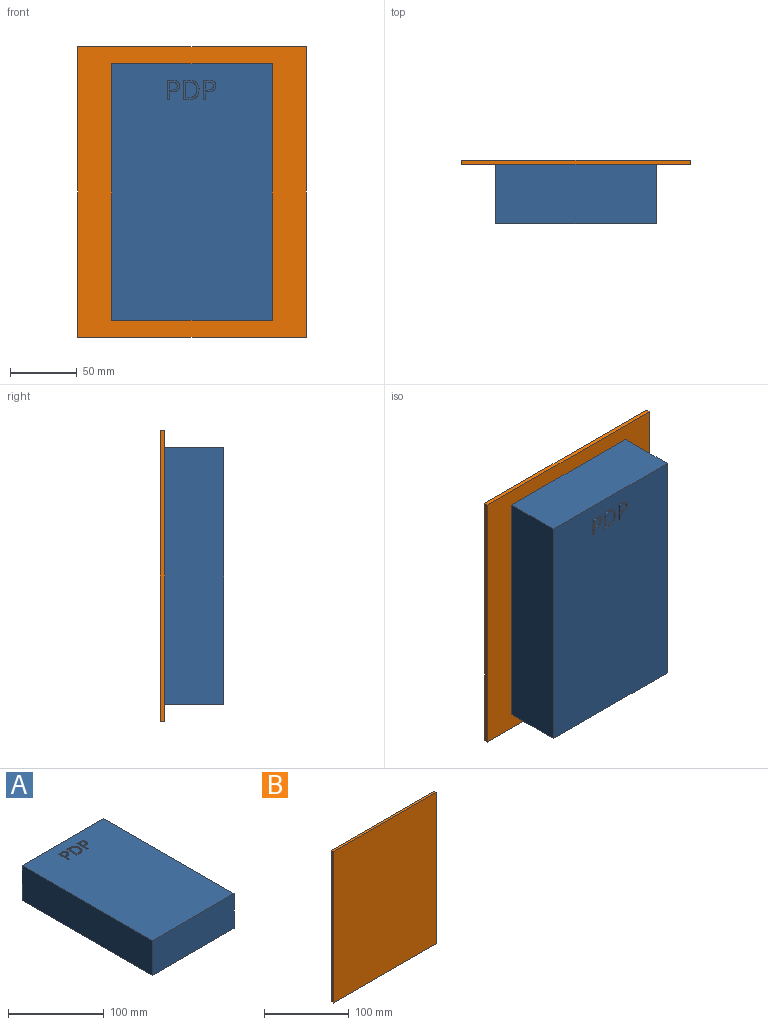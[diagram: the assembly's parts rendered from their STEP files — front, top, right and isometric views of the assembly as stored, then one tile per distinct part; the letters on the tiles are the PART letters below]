
ASSEMBLY  parts=2 mates=1
PART A: 56 faces, bbox 120.9x192.7x44.5 mm
  f0: plane 192.68x120.88mm, normal (0,0,1), area 22972.2mm2, adj f1,f2,f3,f4,f12,f13,f14,f15
  f1: plane 192.68x44.45mm, normal (1,0,0), area 8564.8mm2, adj f0,f2,f4,f5
  f2: plane 120.88x44.45mm, normal (0,1,0), area 5373.1mm2, adj f0,f1,f3,f5
  f3: plane 192.68x44.45mm, normal (-1,0,0), area 8564.8mm2, adj f0,f2,f4,f5
  f4: plane 120.88x44.45mm, normal (0,-1,0), area 5373.1mm2, adj f0,f1,f3,f5
  f5: plane 192.68x120.88mm, normal (0,0,-1), area 23291.4mm2, adj f1,f2,f3,f4
  f6: plane 1.54x1.27mm, normal (0,-1,0), area 1.9mm2, adj f7,f20,f21,f53
  f7: plane 5.95x1.27mm, normal (-1,0,0), area 7.6mm2, adj f6,f8,f21,f53
  f8: plane 1.9x1.27mm, normal (0,1,0), area 2.4mm2, adj f7,f9,f21,f53
  f9: extruded ~2.96x1.27mm, area 3.9mm2, adj f8,f10,f21,f53
  f10: extruded ~2.16x1.27mm, area 3.1mm2, adj f9,f11,f21,f53
  f11: extruded ~2.35x1.27mm, area 3.4mm2, adj f10,f20,f21,f53
  f12: extruded ~3.42x1.52mm, area 4.9mm2, adj f0,f13,f19,f21
  f13: extruded ~5.49x4.27mm, area 10.1mm2, adj f0,f12,f14,f21
  f14: plane 3.8x1.27mm, normal (0,-1,0), area 4.8mm2, adj f0,f13,f15,f21
  f15: plane 14.64x1.27mm, normal (1,0,0), area 18.6mm2, adj f0,f14,f16,f21
  f16: plane 1.7x1.27mm, normal (0,1,0), area 2.2mm2, adj f0,f15,f17,f21
  f17: plane 5.76x1.27mm, normal (-1,0,0), area 7.3mm2, adj f0,f16,f18,f21
  f18: plane 1.72x1.27mm, normal (0,1,0), area 2.2mm2, adj f0,f17,f19,f21
  f19: extruded ~4.34x1.27mm, area 5.8mm2, adj f0,f12,f18,f21
  f20: extruded ~3.27x1.27mm, area 4.3mm2, adj f6,f11,f21,f53
  f21: plane 14.64x9.29mm, normal (0,0,1), area 52.9mm2, adj f6,f7,f8,f9,f10,f11,f12,f13
  f22: extruded ~4.32x1.44mm, area 5.9mm2, adj f23,f35,f36,f54
  f23: extruded ~4.43x1.53mm, area 6.1mm2, adj f22,f24,f36,f54
  f24: extruded ~4.58x1.5mm, area 6.3mm2, adj f23,f25,f36,f54
  f25: plane 2.07x1.27mm, normal (0,-1,0), area 2.6mm2, adj f24,f26,f36,f54
  f26: plane 11.7x1.27mm, normal (-1,0,0), area 14.9mm2, adj f25,f27,f36,f54
  f27: plane 2.47x1.27mm, normal (0,1,0), area 3.1mm2, adj f26,f35,f36,f54
  f28: extruded ~5.54x1.97mm, area 7.7mm2, adj f0,f29,f34,f36
  f29: extruded ~5.29x1.89mm, area 7.3mm2, adj f0,f28,f30,f36
  f30: extruded ~5.31x1.89mm, area 7.4mm2, adj f0,f29,f31,f36
  f31: plane 4.49x1.27mm, normal (0,-1,0), area 5.7mm2, adj f0,f30,f32,f36
  f32: plane 14.64x1.27mm, normal (1,0,0), area 18.6mm2, adj f0,f31,f33,f36
  f33: plane 4.06x1.27mm, normal (0,1,0), area 5.2mm2, adj f0,f32,f34,f36
  f34: extruded ~5.66x1.92mm, area 7.8mm2, adj f0,f28,f33,f36
  f35: extruded ~4.27x1.45mm, area 5.9mm2, adj f22,f27,f36,f54
  f36: plane 14.64x11.69mm, normal (0,0,1), area 67.8mm2, adj f22,f23,f24,f25,f26,f27,f28,f29
  f37: plane 1.54x1.27mm, normal (0,-1,0), area 1.9mm2, adj f38,f51,f52,f55
  f38: plane 5.95x1.27mm, normal (-1,0,0), area 7.6mm2, adj f37,f39,f52,f55
  f39: plane 1.9x1.27mm, normal (0,1,0), area 2.4mm2, adj f38,f40,f52,f55
  f40: extruded ~2.96x1.27mm, area 3.9mm2, adj f39,f41,f52,f55
  f41: extruded ~2.16x1.27mm, area 3.1mm2, adj f40,f42,f52,f55
  f42: extruded ~2.35x1.27mm, area 3.4mm2, adj f41,f51,f52,f55
  f43: extruded ~3.42x1.52mm, area 4.9mm2, adj f0,f44,f50,f52
  f44: extruded ~5.49x4.27mm, area 10.1mm2, adj f0,f43,f45,f52
  f45: plane 3.8x1.27mm, normal (0,-1,0), area 4.8mm2, adj f0,f44,f46,f52
  f46: plane 14.64x1.27mm, normal (1,0,0), area 18.6mm2, adj f0,f45,f47,f52
  f47: plane 1.7x1.27mm, normal (0,1,0), area 2.2mm2, adj f0,f46,f48,f52
  f48: plane 5.76x1.27mm, normal (-1,0,0), area 7.3mm2, adj f0,f47,f49,f52
  f49: plane 1.72x1.27mm, normal (0,1,0), area 2.2mm2, adj f0,f48,f50,f52
  f50: extruded ~4.34x1.27mm, area 5.8mm2, adj f0,f43,f49,f52
  f51: extruded ~3.27x1.27mm, area 4.3mm2, adj f37,f42,f52,f55
  f52: plane 14.64x9.29mm, normal (0,0,1), area 52.9mm2, adj f37,f38,f39,f40,f41,f42,f43,f44
  f53: plane 5.95x5.82mm, normal (0,0,1), area 30.8mm2, adj f6,f7,f8,f9,f10,f11,f20
  f54: plane 11.7x8.19mm, normal (0,0,1), area 84.1mm2, adj f22,f23,f24,f25,f26,f27,f35
  f55: plane 5.95x5.82mm, normal (0,0,1), area 30.8mm2, adj f37,f38,f39,f40,f41,f42,f51
PART B: 6 faces, bbox 171.7x3.2x218.1 mm
  f0: plane 218.08x3.18mm, normal (1,0,0), area 692.4mm2, adj f1,f3,f4,f5
  f1: plane 171.68x3.18mm, normal (0,0,1), area 545.1mm2, adj f0,f2,f4,f5
  f2: plane 218.08x3.18mm, normal (-1,0,0), area 692.4mm2, adj f1,f3,f4,f5
  f3: plane 171.68x3.18mm, normal (0,0,-1), area 545.1mm2, adj f0,f2,f4,f5
  f4: plane 218.08x171.68mm, normal (0,-1,0), area 37440.4mm2, adj f0,f1,f2,f3
  f5: plane 218.08x171.68mm, normal (0,1,0), area 37440.4mm2, adj f0,f1,f2,f3
PLACE A rot(axis=(1,0,0),90deg) t=(0,-3.18,0)mm
PLACE B at identity fixed
MATE fastened A.f5 <-> B.f4  axis (0,1,0) through (0,-3.18,0)mm
